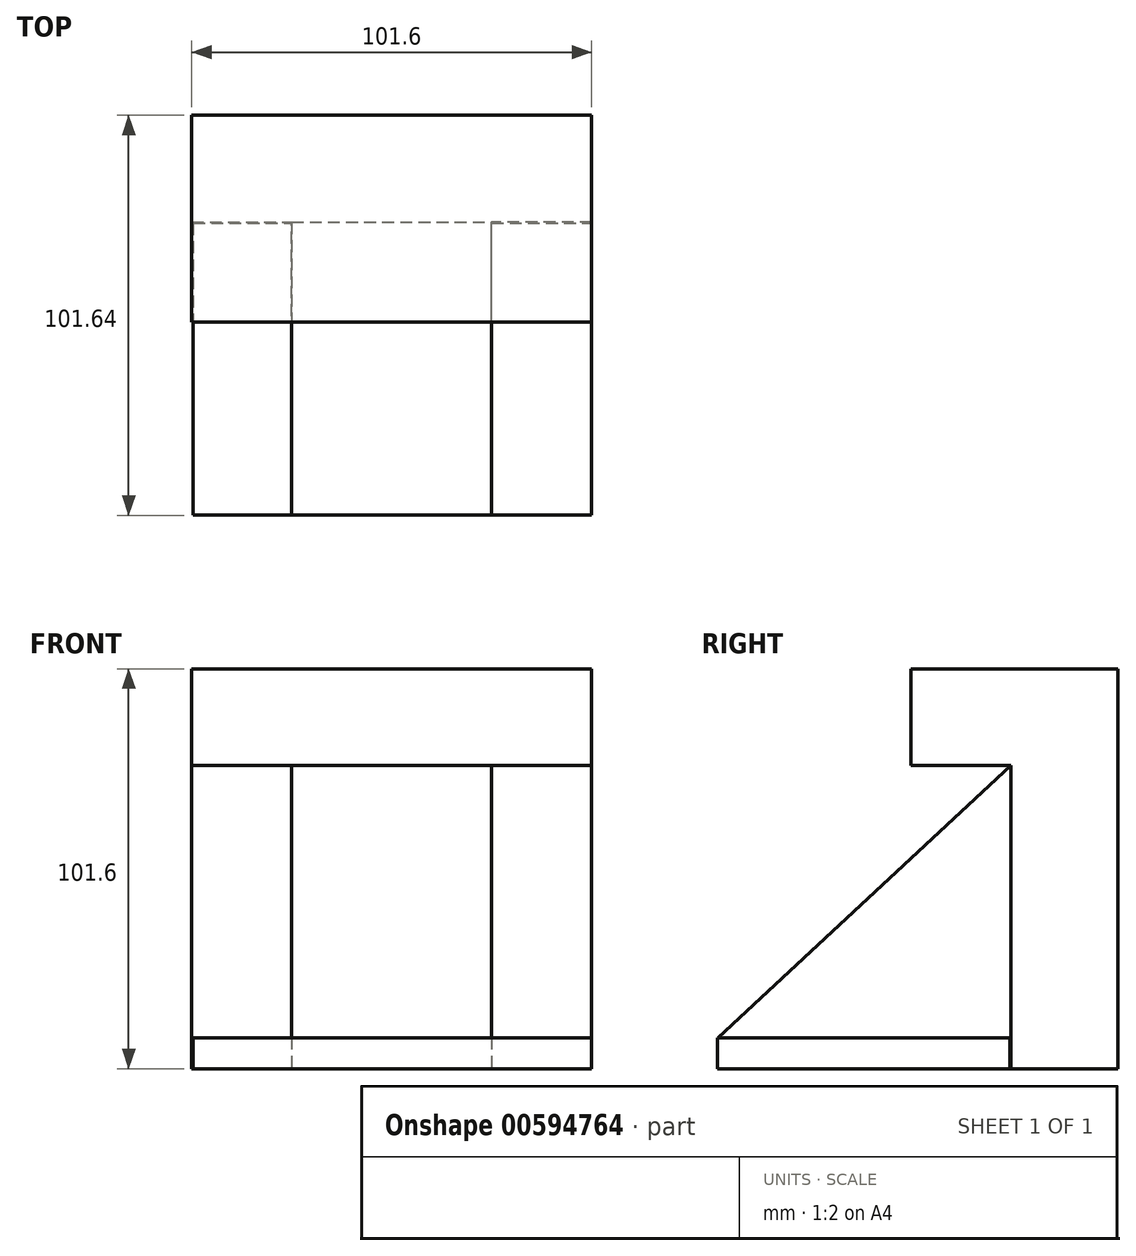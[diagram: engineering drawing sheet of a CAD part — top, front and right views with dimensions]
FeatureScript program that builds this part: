
annotation { "Feature Type Name" : "Feature", "Feature Type Description" : "" }
export const myFeature = defineFeature(function(context is Context, id is Id, definition is map)
    precondition{}
    {
        {
            var Q0;
            Q0=qCreatedBy(makeId("Top.planeOp"),FACE);
            var sketch = newSketch(context, id + "F0", { "sketchPlane" : qUnion([Q0])});
            skLineSegment(sketch, "E0.bottom", {"start": v(0, 0) * mm, "end": v(-101.6, 0) * mm});
            skLineSegment(sketch, "E0.top", {"start": v(0, -101.6) * mm, "end": v(-101.6, -101.6) * mm});
            skLineSegment(sketch, "E0.left", {"start": v(0, 0) * mm, "end": v(0, -101.6) * mm});
            skLineSegment(sketch, "E0.right", {"start": v(-101.6, 0) * mm, "end": v(-101.6, -101.6) * mm});
            skSolve(sketch);
        }
        {
            var Q0;
            Q0=makeQuery(id+"F0.imprint","IMPRINT",FACE,{"disambiguationData":[TD([[makeQuery(id+"F0.imprint","IMPRINT",EDGE,{"derivedFrom":sQuery(id+"F0.wireOp",EDGE,"E0.bottom")}),1.0]])]});
            extrude(context, id + "F1", {"entities" : qUnion([Q0]), "depth" : 101.6 * mm, "offsetDistance" : 25.4 * mm});
        }
        {
            var Q0;
            Q0=makeQuery(id+"F1.opExtrude","SWEPT_FACE",FACE,{"disambiguationData":[OSD([sQuery(id+"F0.wireOp",EDGE,"E0.top")])]});
            var sketch = newSketch(context, id + "F2", { "sketchPlane" : qUnion([Q0])});
            skLineSegment(sketch, "E1.bottom", {"start": v(-101.6, 101.6) * mm, "end": v(-76.2, 101.6) * mm});
            skLineSegment(sketch, "E1.top", {"start": v(-101.6, 0) * mm, "end": v(-76.2, 0) * mm});
            skLineSegment(sketch, "E1.left", {"start": v(-101.6, 101.6) * mm, "end": v(-101.6, 0) * mm});
            skLineSegment(sketch, "E1.right", {"start": v(-76.2, 101.6) * mm, "end": v(-76.2, 0) * mm});
            skLineSegment(sketch, "E2.bottom", {"start": v(-76.2, 101.6) * mm, "end": v(-50.8, 101.6) * mm});
            skLineSegment(sketch, "E2.top", {"start": v(-76.2, 0) * mm, "end": v(-50.8, 0) * mm});
            skLineSegment(sketch, "E2.right", {"start": v(-50.8, 101.6) * mm, "end": v(-50.8, 0) * mm});
            skLineSegment(sketch, "E3.bottom", {"start": v(-50.8, 101.6) * mm, "end": v(-25.4, 101.6) * mm});
            skLineSegment(sketch, "E3.top", {"start": v(-50.8, 0) * mm, "end": v(-25.4, 0) * mm});
            skLineSegment(sketch, "E3.right", {"start": v(-25.4, 101.6) * mm, "end": v(-25.4, 0) * mm});
            skLineSegment(sketch, "E4.bottom", {"start": v(-25.4, 101.6) * mm, "end": v(0, 101.6) * mm});
            skLineSegment(sketch, "E4.top", {"start": v(-25.4, 0) * mm, "end": v(0, 0) * mm});
            skLineSegment(sketch, "E4.right", {"start": v(0, 101.6) * mm, "end": v(0, 0) * mm});
            skSolve(sketch);
        }
        {
            var Q0;
            Q0=makeQuery(id+"F2.imprint","IMPRINT",FACE,{"disambiguationData":[TD([[makeQuery(id+"F2.imprint","IMPRINT",EDGE,{"derivedFrom":sQuery(id+"F2.wireOp",EDGE,"E4.bottom")}),1.0]])]});
            var Q1;
            Q1=makeQuery(id+"F2.imprint","IMPRINT",FACE,{"disambiguationData":[TD([[makeQuery(id+"F2.imprint","IMPRINT",EDGE,{"derivedFrom":sQuery(id+"F2.wireOp",EDGE,"E1.bottom")}),1.0]])]});
            extrude(context, id + "F3", {"entities" : qUnion([Q0, Q1]), "operationType" : NewBodyOperationType.REMOVE, "oppositeDirection" : true, "depth" : 74.42 * mm, "offsetDistance" : 25.4 * mm});
        }
        {
            var Q0;
            Q0=qCreatedBy(makeId("Top.planeOp"),FACE);
            var sketch = newSketch(context, id + "F4", { "sketchPlane" : qUnion([Q0])});
            skLineSegment(sketch, "E5.bottom", {"start": v(-101.2, -27.43) * mm, "end": v(0, -27.43) * mm});
            skLineSegment(sketch, "E5.top", {"start": v(-101.2, -101.64) * mm, "end": v(0, -101.64) * mm});
            skLineSegment(sketch, "E5.left", {"start": v(-101.2, -27.43) * mm, "end": v(-101.2, -101.64) * mm});
            skLineSegment(sketch, "E5.right", {"start": v(0, -27.43) * mm, "end": v(0, -101.64) * mm});
            skSolve(sketch);
        }
        {
            var Q0;
            Q0=makeQuery(id+"F4.imprint","IMPRINT",FACE,{"disambiguationData":[TD([[makeQuery(id+"F4.imprint","IMPRINT",EDGE,{"derivedFrom":sQuery(id+"F4.wireOp",EDGE,"E5.bottom")}),-1.0]])]});
            extrude(context, id + "F5", {"entities" : qUnion([Q0]), "operationType" : NewBodyOperationType.ADD, "depth" : 7.87 * mm, "offsetDistance" : 25.4 * mm});
        }
        {
            var Q0;
            Q0=makeQuery(id+"F3.boolean.opBoolean","COPY",FACE,{"derivedFrom":makeQuery(id+"F3.opExtrude","SWEPT_FACE",FACE,{"disambiguationData":[OSD([sQuery(id+"F2.wireOp",EDGE,"E3.right")])]})});
            var sketch = newSketch(context, id + "F6", { "sketchPlane" : qUnion([Q0])});
            skLineSegment(sketch, "E6", {"start": v(-101.6, 7.87) * mm, "end": v(-27.18, 77.04) * mm});
            skSolve(sketch);
        }
        {
            var Q0;
            {var subQ0=sQuery(id+"F6.wireOp",EDGE,"E6");Q0=makeQuery(id+"F6.imprint","IMPRINT",FACE,{"disambiguationData":[TD([[makeQuery(id+"F6.imprint","IMPRINT",EDGE,{"derivedFrom":subQ0}),1.0]])]});}
            extrude(context, id + "F7", {"entities" : qUnion([Q0]), "operationType" : NewBodyOperationType.REMOVE, "oppositeDirection" : true, "depth" : 102.62 * mm, "offsetDistance" : 25.4 * mm});
        }
        {
            var Q0;
            {var subQ0=sQuery(id+"F2.wireOp",EDGE,"E3.right");var subQ1=makeQuery(id+"F3.boolean.opBoolean","COPY",EDGE,{"derivedFrom":makeQuery(id+"F3.opExtrude","CAP_EDGE",EDGE,{"disambiguationData":[OSD([subQ0])],"isStart":false})});var subQ2=sQuery(id+"F2.wireOp",EDGE,"E4.bottom");Q0=makeQuery(id+"F7.boolean.opBoolean","MERGE",FACE,{"derivedFrom":[makeQuery(id+"F3.boolean.opBoolean","COPY",FACE,{"derivedFrom":makeQuery(id+"F3.opExtrude","CAP_FACE",FACE,{"disambiguationData":[OSD([sQuery(id+"F2.wireOp",EDGE,"E1.bottom"),sQuery(id+"F2.wireOp",EDGE,"E1.top"),sQuery(id+"F2.wireOp",EDGE,"E1.left"),sQuery(id+"F2.wireOp",EDGE,"E1.right")])],"isStart":false})}),makeQuery(id+"F3.boolean.opBoolean","COPY",FACE,{"derivedFrom":makeQuery(id+"F3.opExtrude","CAP_FACE",FACE,{"disambiguationData":[OSD([subQ2,sQuery(id+"F2.wireOp",EDGE,"E4.top"),subQ0,sQuery(id+"F2.wireOp",EDGE,"E4.right")])],"isStart":false})}),makeQuery(id+"F7.opExtrude","SWEPT_FACE",FACE,{"disambiguationData":[OSD([subQ0]),TDD([makeQuery(id+"F6.imprint","IMPRINT",EDGE,{"disambiguationData":[TD([[makeQuery(id+"F6.imprint","INTERSECT",VERTEX,{"derivedFrom":[subQ1,sQuery(id+"F6.wireOp",EDGE,"E6")]}),1.0]])],"derivedFrom":subQ1})])]})]});}
            var sketch = newSketch(context, id + "F8", { "sketchPlane" : qUnion([Q0])});
            skLineSegment(sketch, "E7.bottom", {"start": v(-101.6, 101.6) * mm, "end": v(0, 101.6) * mm});
            skLineSegment(sketch, "E7.top", {"start": v(-101.6, 77.04) * mm, "end": v(0, 77.04) * mm});
            skLineSegment(sketch, "E7.left", {"start": v(-101.6, 101.6) * mm, "end": v(-101.6, 77.04) * mm});
            skLineSegment(sketch, "E7.right", {"start": v(0, 101.6) * mm, "end": v(0, 77.04) * mm});
            skSolve(sketch);
        }
        {
            var Q0;
            Q0=makeQuery(id+"F8.imprint","IMPRINT",FACE,{"disambiguationData":[TD([[makeQuery(id+"F8.imprint","IMPRINT",EDGE,{"derivedFrom":sQuery(id+"F8.wireOp",EDGE,"E7.bottom")}),1.0]])]});
            extrude(context, id + "F9", {"entities" : qUnion([Q0]), "operationType" : NewBodyOperationType.ADD, "depth" : 25.4 * mm, "offsetDistance" : 25.4 * mm});
        }
    });
